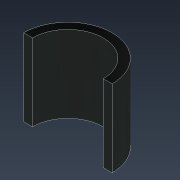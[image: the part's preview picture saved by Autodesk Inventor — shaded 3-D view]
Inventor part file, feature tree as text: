
AUTODESK INVENTOR PART (.ipt)
format: ipt  version: 2022 (Build 260153000, 153)  size: 87,552 bytes
history: native  units: mm
features: extrude x1, sketch x1
ambient origin geometry x8: Origin, YZ Plane, XZ Plane, XY Plane, X Axis, Y Axis, Z Axis, Center Point
bodies: Solid1 (feature_tree)
feature tree (2):
  extrude  "Extrusion1"  Depth=21.76mm
  sketch  "Sketch1"  dims[d0=20.0mm d1=25.0mm d2=21.76mm d3=0.0mm]
